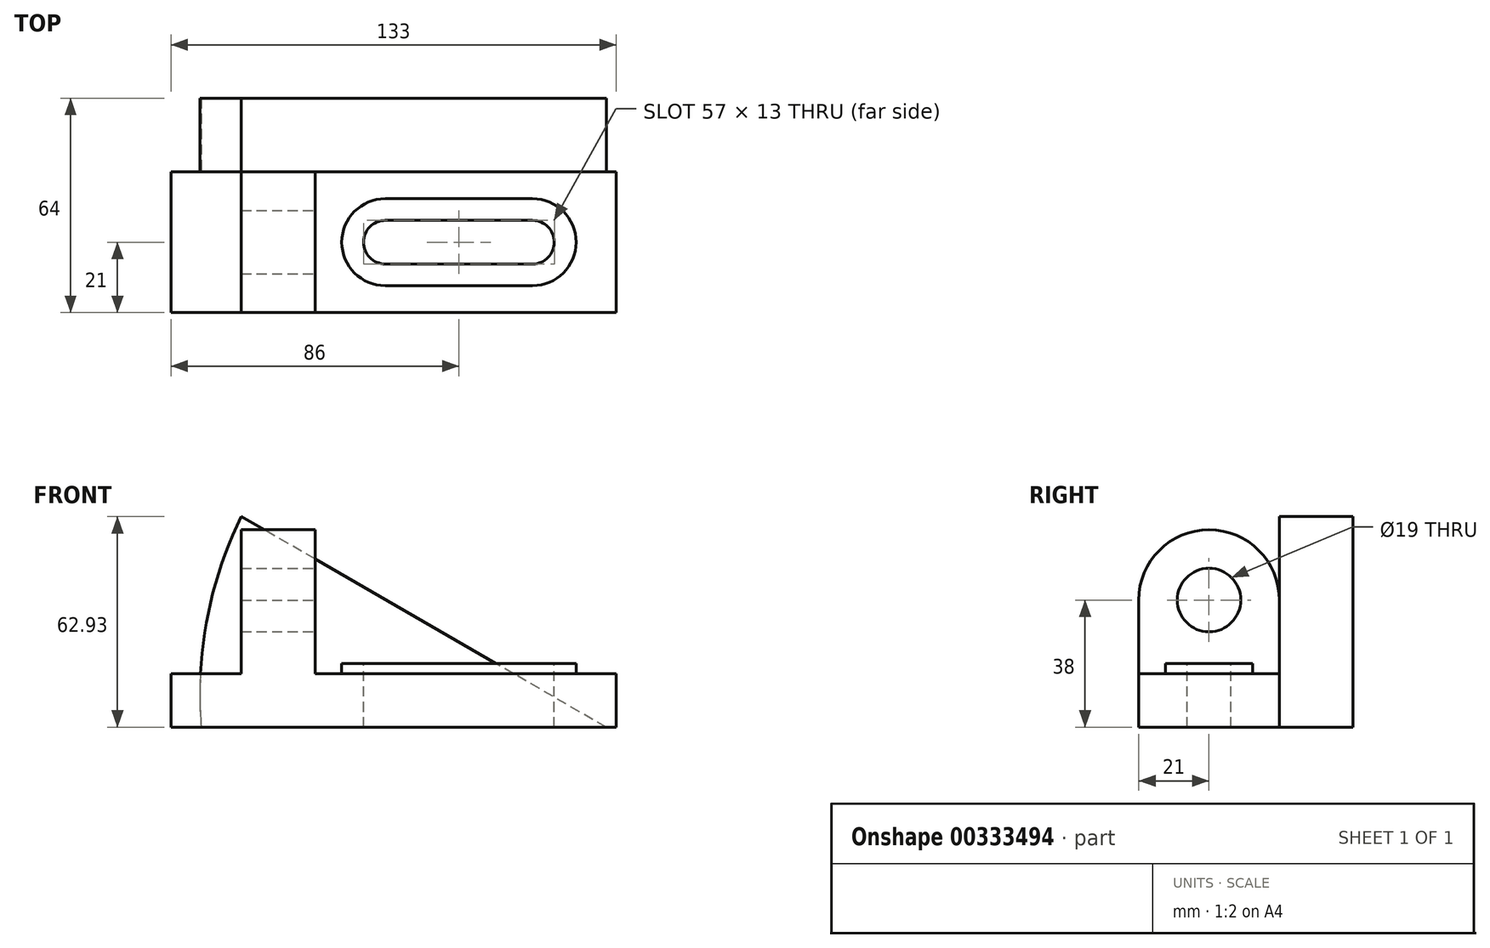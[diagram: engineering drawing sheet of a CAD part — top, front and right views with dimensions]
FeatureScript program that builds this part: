
annotation { "Feature Type Name" : "Feature", "Feature Type Description" : "" }
export const myFeature = defineFeature(function(context is Context, id is Id, definition is map)
    precondition{}
    {
        {
            var Q0;
            Q0=qCreatedBy(makeId("Front.planeOp"),FACE);
            var sketch = newSketch(context, id + "F0", { "sketchPlane" : qUnion([Q0])});
            skLineSegment(sketch, "E0", {"start": v(0, 0) * mm, "end": v(133, 0) * mm});
            skLineSegment(sketch, "E1", {"start": v(133, 0) * mm, "end": v(133, 16) * mm});
            skLineSegment(sketch, "E2", {"start": v(133, 16) * mm, "end": v(43, 16) * mm});
            skLineSegment(sketch, "E3", {"start": v(43, 16) * mm, "end": v(43, 60) * mm});
            skLineSegment(sketch, "E4", {"start": v(43, 60) * mm, "end": v(21, 60) * mm});
            skLineSegment(sketch, "E5", {"start": v(21, 60) * mm, "end": v(21, 16) * mm});
            skLineSegment(sketch, "E6", {"start": v(21, 16) * mm, "end": v(0, 16) * mm});
            skLineSegment(sketch, "E7", {"start": v(0, 16) * mm, "end": v(0, 0) * mm});
            skSolve(sketch);
        }
        {
            var Q0;
            Q0 = qSketchRegion(id + "F0", true);
            extrude(context, id + "F1", {"entities" : qUnion([Q0]), "depth" : 42 * mm});
        }
        {
            var Q0;
            Q0=makeQuery(id+"F1.opExtrude","SWEPT_FACE",FACE,{"disambiguationData":[OSD([sQuery(id+"F0.wireOp",EDGE,"E3")])]});
            var sketch = newSketch(context, id + "F2", { "sketchPlane" : qUnion([Q0])});
            skCircle(sketch, "E8", {"center": v(-21, 38) * mm, "radius": 9.5 * mm});
            skLineSegment(sketch, "E9", {"start": v(-21, 16) * mm, "end": v(-21, 60) * mm, "construction": true});
            skSolve(sketch);
        }
        {
            var Q0;
            Q0 = qSketchRegion(id + "F2", true);
            extrude(context, id + "F3", {"entities" : qUnion([Q0]), "operationType" : NewBodyOperationType.REMOVE, "endBound" : BoundingType.THROUGH_ALL, "oppositeDirection" : true, "depth" : 25 * mm});
        }
        {
            var Q0;
            Q0=makeQuery(id+"F1.opExtrude","SWEPT_FACE",FACE,{"disambiguationData":[OSD([sQuery(id+"F0.wireOp",EDGE,"E3")])]});
            var sketch = newSketch(context, id + "F4", { "sketchPlane" : qUnion([Q0])});
            skPoint(sketch, "E10", {"position": v(-21, 38) * mm});
            skArc(sketch, "E11", {"start": v(-42, 38) * mm, "mid": v(-21, 59) * mm, "end": v(0, 38) * mm});
            skLineSegment(sketch, "E12", {"start": v(-42, 38) * mm, "end": v(-42, 60) * mm});
            skLineSegment(sketch, "E13", {"start": v(-42, 60) * mm, "end": v(0, 60) * mm});
            skLineSegment(sketch, "E14", {"start": v(0, 60) * mm, "end": v(0, 38) * mm});
            skSolve(sketch);
        }
        {
            var Q0;
            Q0 = qSketchRegion(id + "F4", true);
            extrude(context, id + "F5", {"entities" : qUnion([Q0]), "operationType" : NewBodyOperationType.REMOVE, "endBound" : BoundingType.THROUGH_ALL, "oppositeDirection" : true, "depth" : 25 * mm});
        }
        {
            var Q0;
            Q0=makeQuery(id+"F1.opExtrude","SWEPT_FACE",FACE,{"disambiguationData":[OSD([sQuery(id+"F0.wireOp",EDGE,"E2")])]});
            var sketch = newSketch(context, id + "F6", { "sketchPlane" : qUnion([Q0])});
            skLineSegment(sketch, "E15", {"start": v(133, -21) * mm, "end": v(133, -21) * mm});
            skPoint(sketch, "E15.endSnap0", {"position": v(133, -21) * mm});
            skLineSegment(sketch, "E16", {"start": v(64, -8) * mm, "end": v(108, -8) * mm});
            skLineSegment(sketch, "E17", {"start": v(64, -34) * mm, "end": v(108, -34) * mm});
            skArc(sketch, "E18", {"start": v(64, -8) * mm, "mid": v(51, -21) * mm, "end": v(64, -34) * mm});
            skArc(sketch, "E19", {"start": v(108, -8) * mm, "mid": v(121, -21) * mm, "end": v(108, -34) * mm});
            skSolve(sketch);
        }
        {
            var Q0;
            Q0 = qSketchRegion(id + "F6", true);
            extrude(context, id + "F7", {"entities" : qUnion([Q0]), "operationType" : NewBodyOperationType.ADD, "depth" : 3 * mm});
        }
        {
            var Q0;
            Q0=makeQuery(id+"F7.opExtrude","CAP_FACE",FACE,{"disambiguationData":[OSD([sQuery(id+"F6.wireOp",EDGE,"E16"),sQuery(id+"F6.wireOp",EDGE,"E17"),sQuery(id+"F6.wireOp",EDGE,"E18"),sQuery(id+"F6.wireOp",EDGE,"E19")])],"isStart":false});
            var sketch = newSketch(context, id + "F8", { "sketchPlane" : qUnion([Q0])});
            skLineSegment(sketch, "E20", {"start": v(64, -14.5) * mm, "end": v(108, -14.5) * mm});
            skLineSegment(sketch, "E21.MirrorCS", {"start": v(64, -27.5) * mm, "end": v(108, -27.5) * mm});
            skArc(sketch, "E22", {"start": v(64, -14.5) * mm, "mid": v(57.5, -21) * mm, "end": v(64, -27.5) * mm});
            skArc(sketch, "E23", {"start": v(108, -14.5) * mm, "mid": v(114.5, -21) * mm, "end": v(108, -27.5) * mm});
            skSolve(sketch);
        }
        {
            var Q0;
            Q0 = qSketchRegion(id + "F8", true);
            extrude(context, id + "F9", {"entities" : qUnion([Q0]), "operationType" : NewBodyOperationType.REMOVE, "endBound" : BoundingType.THROUGH_ALL, "oppositeDirection" : true, "depth" : 25 * mm});
        }
        {
            var Q0;
            Q0=makeQuery(id+"F1.opExtrude","CAP_FACE",FACE,{"disambiguationData":[OSD([sQuery(id+"F0.wireOp",EDGE,"E0"),sQuery(id+"F0.wireOp",EDGE,"E1"),sQuery(id+"F0.wireOp",EDGE,"E2"),sQuery(id+"F0.wireOp",EDGE,"E3"),sQuery(id+"F0.wireOp",EDGE,"E4"),sQuery(id+"F0.wireOp",EDGE,"E5"),sQuery(id+"F0.wireOp",EDGE,"E6"),sQuery(id+"F0.wireOp",EDGE,"E7")])],"isStart":true});
            var sketch = newSketch(context, id + "F10", { "sketchPlane" : qUnion([Q0])});
            skLineSegment(sketch, "E24", {"start": v(-130, 0) * mm, "end": v(-21, 62.93) * mm});
            skLineSegment(sketch, "E25", {"start": v(-130, 0) * mm, "end": v(-9, 0) * mm});
            skArc(sketch, "E26", {"start": v(-9, 0) * mm, "mid": v(-10.76, 32.27) * mm, "end": v(-21, 62.93) * mm});
            skSolve(sketch);
        }
        {
            var Q0;
            Q0 = qSketchRegion(id + "F10", true);
            extrude(context, id + "F11", {"entities" : qUnion([Q0]), "operationType" : NewBodyOperationType.ADD, "depth" : 22 * mm});
        }
    });
